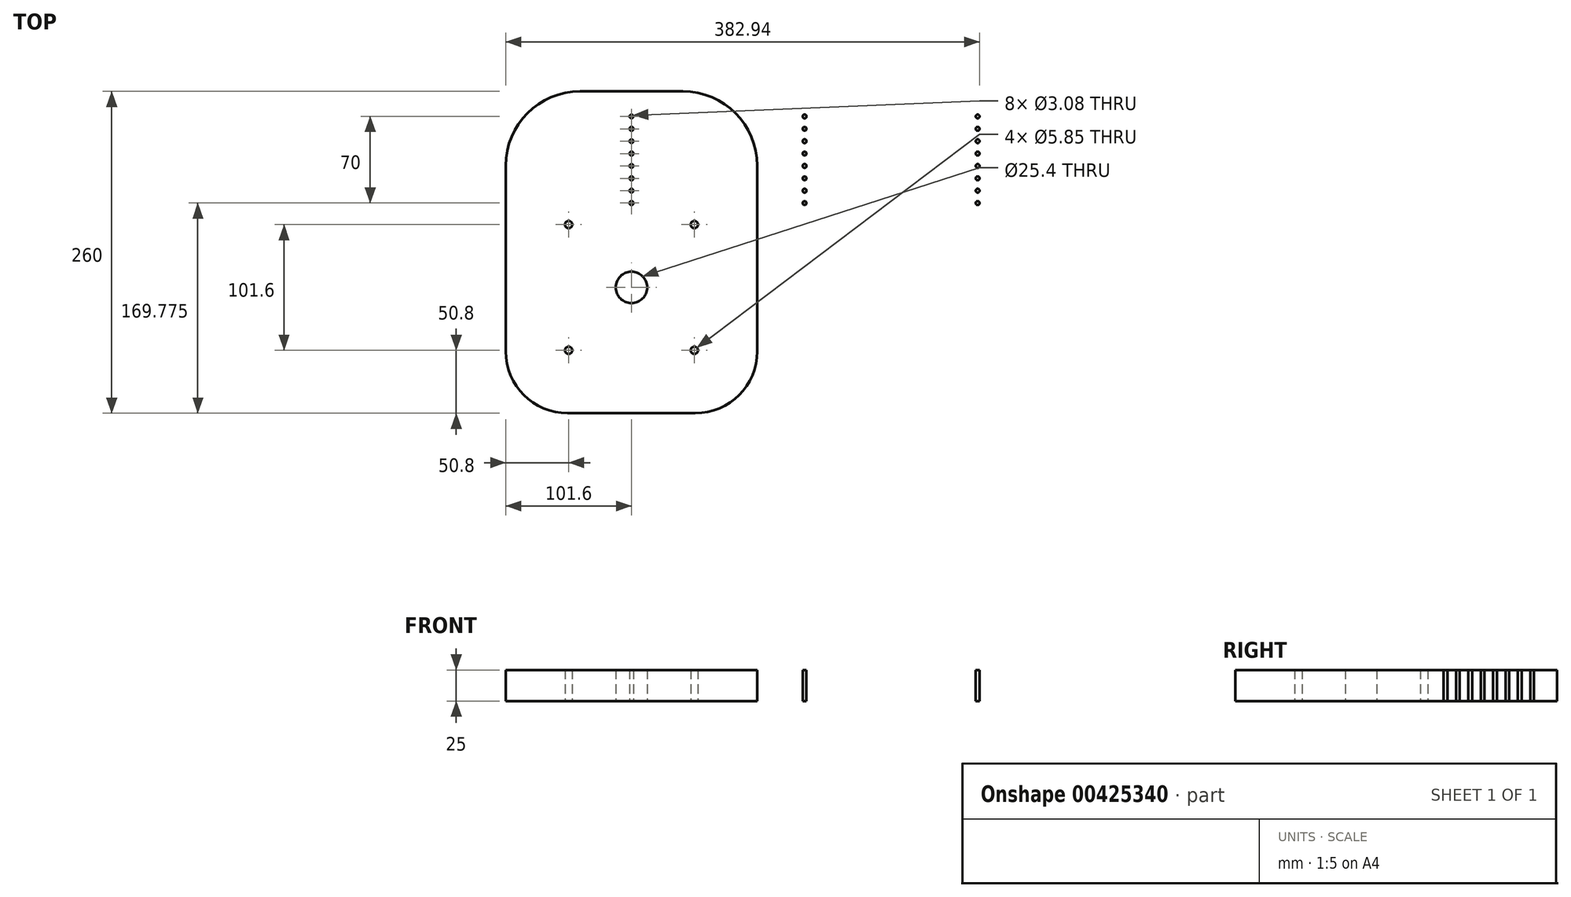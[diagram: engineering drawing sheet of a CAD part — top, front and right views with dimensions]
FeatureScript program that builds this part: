
annotation { "Feature Type Name" : "Feature", "Feature Type Description" : "" }
export const myFeature = defineFeature(function(context is Context, id is Id, definition is map)
    precondition{}
    {
        {
            var Q0;
            Q0=qCreatedBy(makeId("Top.planeOp"),FACE);
            var sketch = newSketch(context, id + "F0", { "sketchPlane" : qUnion([Q0])});
            skLineSegment(sketch, "E0.bottom", {"start": v(0, 0) * mm, "end": v(203.2, 0) * mm});
            skLineSegment(sketch, "E0.top", {"start": v(0, 260) * mm, "end": v(203.2, 260) * mm});
            skLineSegment(sketch, "E0.left", {"start": v(0, 0) * mm, "end": v(0, 260) * mm});
            skLineSegment(sketch, "E0.right", {"start": v(203.2, 0) * mm, "end": v(203.2, 260) * mm});
            skLineSegment(sketch, "E1", {"start": v(101.6, 0) * mm, "end": v(101.6, 260) * mm, "construction": true});
            skCircle(sketch, "E2", {"center": v(101.6, 239.78) * mm, "radius": 1.54 * mm});
            skCircle(sketch, "E3", {"center": v(101.6, 101.6) * mm, "radius": 12.7 * mm});
            skLineSegment(sketch, "E4.bottom", {"start": v(152.4, 152.4) * mm, "end": v(50.8, 152.4) * mm});
            skLineSegment(sketch, "E4.top", {"start": v(152.4, 50.8) * mm, "end": v(50.8, 50.8) * mm});
            skLineSegment(sketch, "E4.left", {"start": v(152.4, 152.4) * mm, "end": v(152.4, 50.8) * mm});
            skLineSegment(sketch, "E4.right", {"start": v(50.8, 152.4) * mm, "end": v(50.8, 50.8) * mm});
            skCircle(sketch, "E5", {"center": v(50.8, 152.4) * mm, "radius": 2.93 * mm});
            skCircle(sketch, "E6", {"center": v(152.4, 152.4) * mm, "radius": 2.93 * mm});
            skCircle(sketch, "E7", {"center": v(50.8, 50.8) * mm, "radius": 2.93 * mm});
            skCircle(sketch, "E8", {"center": v(152.4, 50.8) * mm, "radius": 2.93 * mm});
            skCircle(sketch, "E9.0.1.0", {"center": v(101.6, 229.78) * mm, "radius": 1.54 * mm});
            skCircle(sketch, "E9.0.2.0", {"center": v(101.6, 219.78) * mm, "radius": 1.54 * mm});
            skCircle(sketch, "E9.0.3.0", {"center": v(101.6, 209.77) * mm, "radius": 1.54 * mm});
            skCircle(sketch, "E9.0.4.0", {"center": v(101.6, 199.77) * mm, "radius": 1.54 * mm});
            skCircle(sketch, "E9.0.5.0", {"center": v(101.6, 189.77) * mm, "radius": 1.54 * mm});
            skCircle(sketch, "E9.0.6.0", {"center": v(101.6, 179.77) * mm, "radius": 1.54 * mm});
            skCircle(sketch, "E9.0.7.0", {"center": v(101.6, 169.77) * mm, "radius": 1.54 * mm});
            skCircle(sketch, "E9.1.0.0", {"center": v(241.5, 239.78) * mm, "radius": 1.54 * mm});
            skCircle(sketch, "E9.1.1.0", {"center": v(241.5, 229.78) * mm, "radius": 1.54 * mm});
            skCircle(sketch, "E9.1.2.0", {"center": v(241.5, 219.78) * mm, "radius": 1.54 * mm});
            skCircle(sketch, "E9.1.3.0", {"center": v(241.5, 209.77) * mm, "radius": 1.54 * mm});
            skCircle(sketch, "E9.1.4.0", {"center": v(241.5, 199.77) * mm, "radius": 1.54 * mm});
            skCircle(sketch, "E9.1.5.0", {"center": v(241.5, 189.77) * mm, "radius": 1.54 * mm});
            skCircle(sketch, "E9.1.6.0", {"center": v(241.5, 179.77) * mm, "radius": 1.54 * mm});
            skCircle(sketch, "E9.1.7.0", {"center": v(241.5, 169.77) * mm, "radius": 1.54 * mm});
            skCircle(sketch, "E9.2.0.0", {"center": v(381.4, 239.78) * mm, "radius": 1.54 * mm});
            skCircle(sketch, "E9.2.1.0", {"center": v(381.4, 229.78) * mm, "radius": 1.54 * mm});
            skCircle(sketch, "E9.2.2.0", {"center": v(381.4, 219.78) * mm, "radius": 1.54 * mm});
            skCircle(sketch, "E9.2.3.0", {"center": v(381.4, 209.77) * mm, "radius": 1.54 * mm});
            skCircle(sketch, "E9.2.4.0", {"center": v(381.4, 199.77) * mm, "radius": 1.54 * mm});
            skCircle(sketch, "E9.2.5.0", {"center": v(381.4, 189.77) * mm, "radius": 1.54 * mm});
            skCircle(sketch, "E9.2.6.0", {"center": v(381.4, 179.77) * mm, "radius": 1.54 * mm});
            skCircle(sketch, "E9.2.7.0", {"center": v(381.4, 169.77) * mm, "radius": 1.54 * mm});
            skLineSegment(sketch, "E9.direction1", {"start": v(101.6, 219.78) * mm, "end": v(241.5, 219.78) * mm, "construction": true});
            skLineSegment(sketch, "E9.direction2", {"start": v(101.6, 219.78) * mm, "end": v(101.6, 209.78) * mm, "construction": true});
            skSolve(sketch);
        }
        {
            var Q0;
            Q0 = qSketchRegion(id + "F0", true);
            var Q1;
            Q1=makeQuery(id+"F0.imprint","IMPRINT",FACE,{"disambiguationData":[TD([[makeQuery(id+"F0.imprint","IMPRINT",EDGE,{"derivedFrom":sQuery(id+"F0.wireOp",EDGE,"E3")}),-1.0]])]});
            extrude(context, id + "F1", {"entities" : qUnion([Q0, Q1]), "depth" : 25 * mm, "offsetDistance" : 25 * mm});
        }
        {
            var Q0;
            Q0=makeQuery(id+"F1.opExtrude","SWEPT_EDGE",EDGE,{"disambiguationData":[OSD([sQuery(id+"F0.wireOp",EDGE,"E0.top"),sQuery(id+"F0.wireOp",EDGE,"E0.right")])]});
            var Q1;
            Q1=makeQuery(id+"F1.opExtrude","SWEPT_EDGE",EDGE,{"disambiguationData":[OSD([sQuery(id+"F0.wireOp",EDGE,"E0.top"),sQuery(id+"F0.wireOp",EDGE,"E0.left")])]});
            fillet(context, id + "F2", {"entities" : qUnion([Q0, Q1]), "radius" : 60 * mm, "tangentPropagation" : true, "allowEdgeOverflow" : false});
        }
        {
            var Q0;
            Q0=makeQuery(id+"F1.opExtrude","SWEPT_EDGE",EDGE,{"disambiguationData":[OSD([sQuery(id+"F0.wireOp",EDGE,"E0.bottom"),sQuery(id+"F0.wireOp",EDGE,"E0.right")])]});
            var Q1;
            Q1=makeQuery(id+"F1.opExtrude","SWEPT_EDGE",EDGE,{"disambiguationData":[OSD([sQuery(id+"F0.wireOp",EDGE,"E0.bottom"),sQuery(id+"F0.wireOp",EDGE,"E0.left")])]});
            fillet(context, id + "F3", {"entities" : qUnion([Q0, Q1]), "radius" : 50 * mm, "tangentPropagation" : true, "allowEdgeOverflow" : false});
        }
    });
